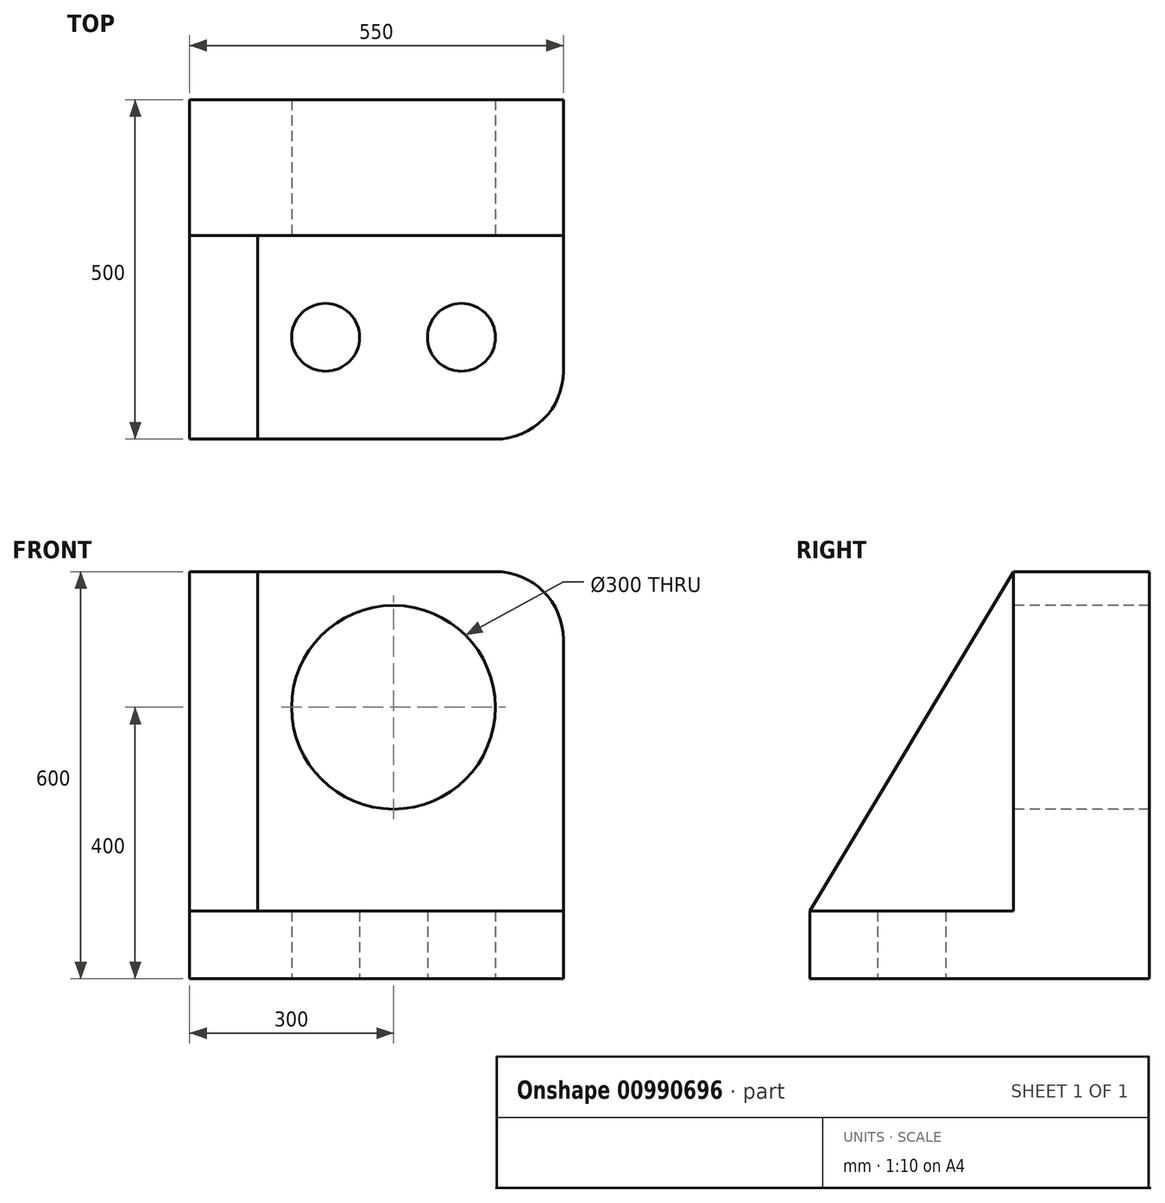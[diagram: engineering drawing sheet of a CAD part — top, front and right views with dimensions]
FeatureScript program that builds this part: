
annotation { "Feature Type Name" : "Feature", "Feature Type Description" : "" }
export const myFeature = defineFeature(function(context is Context, id is Id, definition is map)
    precondition{}
    {
        {
            var Q0;
            Q0=qCreatedBy(makeId("Top.planeOp"),FACE);
            var sketch = newSketch(context, id + "F0", { "sketchPlane" : qUnion([Q0])});
            skLineSegment(sketch, "E0.bottom", {"start": v(175, -250) * mm, "end": v(-275, -250) * mm});
            skLineSegment(sketch, "E0.top", {"start": v(275, 250) * mm, "end": v(-275, 250) * mm});
            skLineSegment(sketch, "E0.left", {"start": v(275, -150) * mm, "end": v(275, 250) * mm});
            skLineSegment(sketch, "E0.right", {"start": v(-275, -250) * mm, "end": v(-275, 250) * mm});
            skPoint(sketch, "E0.middle", {"position": v(0, 0) * mm});
            skPoint(sketch, "E1.visualSharp", {"position": v(275, -250) * mm});
            skArc(sketch, "E1.filletArc", {"start": v(175, -250) * mm, "mid": v(245.71, -220.71) * mm, "end": v(275, -150) * mm});
            skLineSegment(sketch, "E2", {"start": v(-275, 50) * mm, "end": v(275, 50) * mm});
            skLineSegment(sketch, "E3", {"start": v(-175, 50) * mm, "end": v(-175, -250) * mm});
            skCircle(sketch, "E4", {"center": v(-75, -100) * mm, "radius": 50 * mm});
            skCircle(sketch, "E5", {"center": v(125, -100) * mm, "radius": 50 * mm});
            skSolve(sketch);
        }
        {
            var Q0;
            {var subQ4=sQuery(id+"F0.wireOp",EDGE,"E1.filletArc");Q0=makeQuery(id+"F0.imprint","IMPRINT",FACE,{"disambiguationData":[TD([[makeQuery(id+"F0.imprint","IMPRINT",EDGE,{"derivedFrom":subQ4}),1.0]])]});}
            var Q1;
            {var subQ4=sQuery(id+"F0.wireOp",EDGE,"E0.top");Q1=makeQuery(id+"F0.imprint","IMPRINT",FACE,{"disambiguationData":[TD([[makeQuery(id+"F0.imprint","IMPRINT",EDGE,{"derivedFrom":subQ4}),1.0]])]});}
            var Q2;
            {var subQ3=sQuery(id+"F0.wireOp",EDGE,"E3");Q2=makeQuery(id+"F0.imprint","IMPRINT",FACE,{"disambiguationData":[TD([[makeQuery(id+"F0.imprint","IMPRINT",EDGE,{"derivedFrom":subQ3}),-1.0]])]});}
            extrude(context, id + "F1", {"entities" : qUnion([Q0, Q1, Q2]), "depth" : 100 * mm, "offsetDistance" : 25 * mm});
        }
        {
            var Q0;
            {var subQ4=sQuery(id+"F0.wireOp",EDGE,"E0.top");Q0=makeQuery(id+"F0.imprint","IMPRINT",FACE,{"disambiguationData":[TD([[makeQuery(id+"F0.imprint","IMPRINT",EDGE,{"derivedFrom":subQ4}),1.0]])]});}
            var Q1;
            {var subQ3=sQuery(id+"F0.wireOp",EDGE,"E3");Q1=makeQuery(id+"F0.imprint","IMPRINT",FACE,{"disambiguationData":[TD([[makeQuery(id+"F0.imprint","IMPRINT",EDGE,{"derivedFrom":subQ3}),-1.0]])]});}
            extrude(context, id + "F2", {"entities" : qUnion([Q0, Q1]), "operationType" : NewBodyOperationType.ADD, "depth" : 600 * mm, "offsetDistance" : 25 * mm});
        }
        {
            var Q0;
            Q0=makeQuery(id+"F2.opExtrude","CAP_EDGE",EDGE,{"disambiguationData":[OSD([sQuery(id+"F0.wireOp",EDGE,"E0.left")])],"isStart":false});
            fillet(context, id + "F3", {"entities" : qUnion([Q0]), "radius" : 100 * mm, "tangentPropagation" : true, "allowEdgeOverflow" : false});
        }
        {
            var Q0;
            Q0=makeQuery(id+"F2.opExtrude","SWEPT_FACE",FACE,{"disambiguationData":[OSD([sQuery(id+"F0.wireOp",EDGE,"E3")])]});
            var sketch = newSketch(context, id + "F4", { "sketchPlane" : qUnion([Q0])});
            skLineSegment(sketch, "E6.0", {"start": v(50, 600) * mm, "end": v(-250, 600) * mm});
            skLineSegment(sketch, "E6.1", {"start": v(50, 600) * mm, "end": v(50, 100) * mm});
            skLineSegment(sketch, "E6.2", {"start": v(-250, 600) * mm, "end": v(-250, 100) * mm});
            skLineSegment(sketch, "E7", {"start": v(-250, 100) * mm, "end": v(50, 600) * mm});
            skSolve(sketch);
        }
        {
            var Q0;
            Q0 = qSketchRegion(id + "F4", true);
            extrude(context, id + "F5", {"entities" : qUnion([Q0]), "operationType" : NewBodyOperationType.REMOVE, "oppositeDirection" : true, "depth" : 100 * mm, "offsetDistance" : 25 * mm});
        }
        {
            var Q0;
            Q0=makeQuery(id+"F2.opExtrude","SWEPT_FACE",FACE,{"disambiguationData":[OSD([sQuery(id+"F0.wireOp",EDGE,"E2")])]});
            var sketch = newSketch(context, id + "F6", { "sketchPlane" : qUnion([Q0])});
            skCircle(sketch, "E8", {"center": v(25, 400) * mm, "radius": 150 * mm});
            skSolve(sketch);
        }
        {
            var Q0;
            Q0 = qSketchRegion(id + "F6", true);
            extrude(context, id + "F7", {"entities" : qUnion([Q0]), "operationType" : NewBodyOperationType.REMOVE, "oppositeDirection" : true, "depth" : 200 * mm, "offsetDistance" : 25 * mm});
        }
    });
